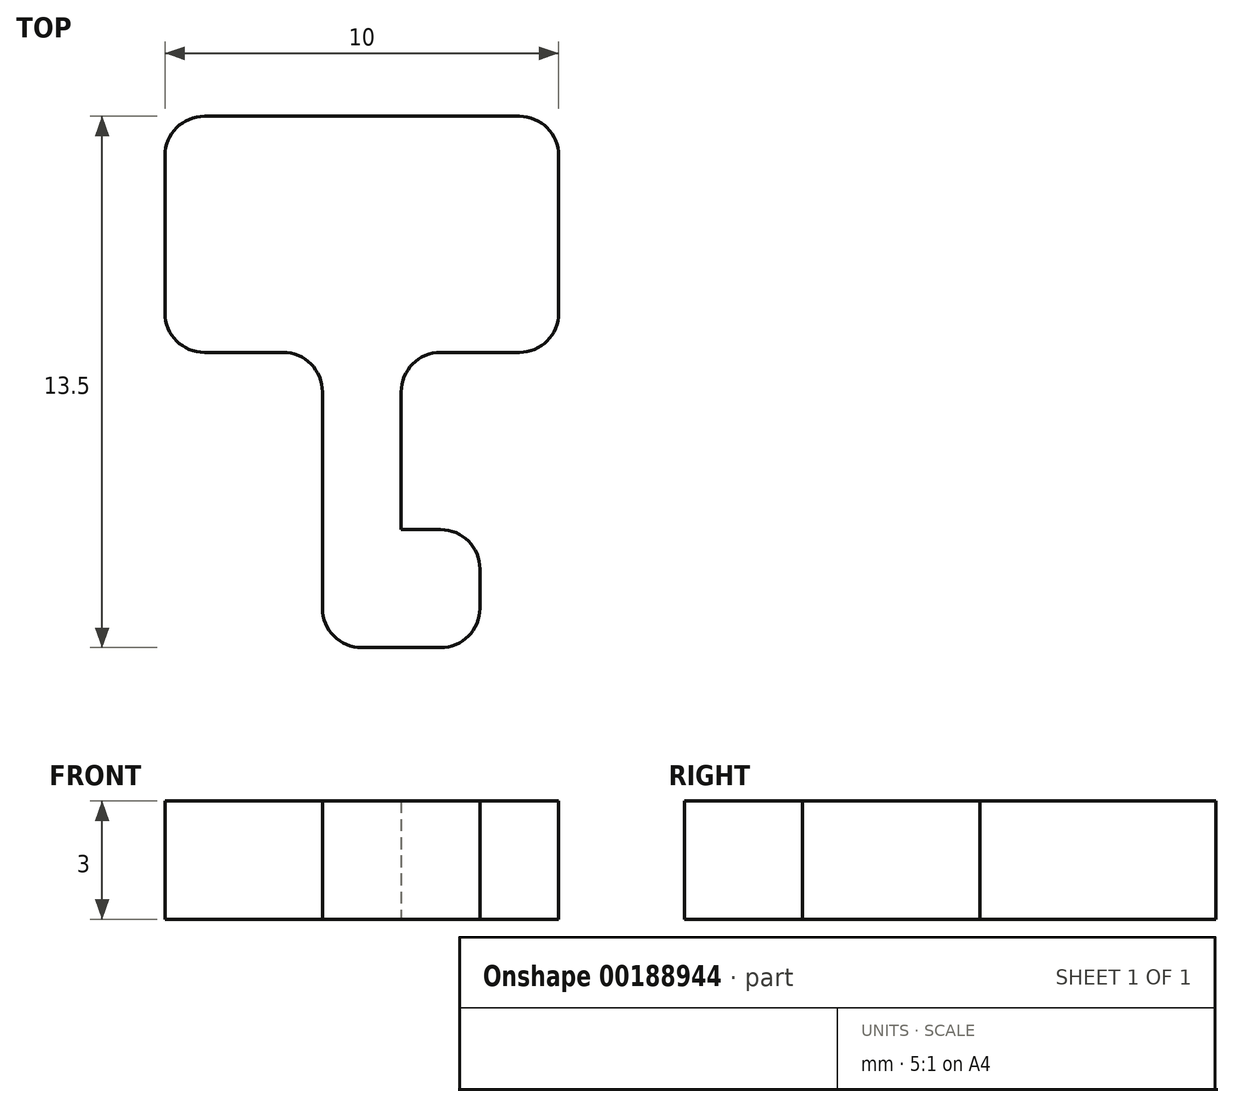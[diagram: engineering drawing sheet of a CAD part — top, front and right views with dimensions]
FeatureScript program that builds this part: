
annotation { "Feature Type Name" : "Feature", "Feature Type Description" : "" }
export const myFeature = defineFeature(function(context is Context, id is Id, definition is map)
    precondition{}
    {
        {
            var Q0;
            Q0=qCreatedBy(makeId("Top.planeOp"),FACE);
            var sketch = newSketch(context, id + "F0", { "sketchPlane" : qUnion([Q0])});
            skLineSegment(sketch, "E0", {"start": v(-1, 0) * mm, "end": v(-3, 0) * mm});
            skLineSegment(sketch, "E1", {"start": v(-4, -1) * mm, "end": v(-4, -4.5) * mm});
            skLineSegment(sketch, "E2", {"start": v(-4, -4.5) * mm, "end": v(-3, -4.5) * mm});
            skLineSegment(sketch, "E3", {"start": v(-2, -5.5) * mm, "end": v(-2, -6.5) * mm});
            skLineSegment(sketch, "E4", {"start": v(-6, -6.5) * mm, "end": v(-6, -1) * mm});
            skLineSegment(sketch, "E5", {"start": v(-7, 0) * mm, "end": v(-9, 0) * mm});
            skLineSegment(sketch, "E6", {"start": v(-10, 1) * mm, "end": v(-10, 5) * mm});
            skLineSegment(sketch, "E7", {"start": v(-9, 6) * mm, "end": v(-1, 6) * mm});
            skLineSegment(sketch, "E8", {"start": v(0, 5) * mm, "end": v(0, 1) * mm});
            skLineSegment(sketch, "E9", {"start": v(-5, -7.5) * mm, "end": v(-3, -7.5) * mm});
            skPoint(sketch, "E10.visualSharp", {"position": v(-6, 0) * mm});
            skArc(sketch, "E10.filletArc", {"start": v(-6, -1) * mm, "mid": v(-6.3, -0.3) * mm, "end": v(-7, 0) * mm});
            skPoint(sketch, "E11.visualSharp", {"position": v(-4, 0) * mm});
            skArc(sketch, "E11.filletArc", {"start": v(-3, 0) * mm, "mid": v(-3.7, -0.3) * mm, "end": v(-4, -1) * mm});
            skPoint(sketch, "E12.visualSharp", {"position": v(0, 0) * mm});
            skArc(sketch, "E12.filletArc", {"start": v(-1, 0) * mm, "mid": v(-0.3, 0.3) * mm, "end": v(0, 1) * mm});
            skPoint(sketch, "E13.visualSharp", {"position": v(0, 6) * mm});
            skArc(sketch, "E13.filletArc", {"start": v(0, 5) * mm, "mid": v(-0.3, 5.7) * mm, "end": v(-1, 6) * mm});
            skPoint(sketch, "E14.visualSharp", {"position": v(-10, 6) * mm});
            skArc(sketch, "E14.filletArc", {"start": v(-9, 6) * mm, "mid": v(-9.7, 5.7) * mm, "end": v(-10, 5) * mm});
            skPoint(sketch, "E15.visualSharp", {"position": v(-10, 0) * mm});
            skArc(sketch, "E15.filletArc", {"start": v(-10, 1) * mm, "mid": v(-9.7, 0.3) * mm, "end": v(-9, 0) * mm});
            skPoint(sketch, "E16.visualSharp", {"position": v(-2, -4.5) * mm});
            skArc(sketch, "E16.filletArc", {"start": v(-2, -5.5) * mm, "mid": v(-2.3, -4.8) * mm, "end": v(-3, -4.5) * mm});
            skPoint(sketch, "E17.visualSharp", {"position": v(-6, -7.5) * mm});
            skArc(sketch, "E17.filletArc", {"start": v(-6, -6.5) * mm, "mid": v(-5.7, -7.2) * mm, "end": v(-5, -7.5) * mm});
            skPoint(sketch, "E18.visualSharp", {"position": v(-2, -7.5) * mm});
            skArc(sketch, "E18.filletArc", {"start": v(-3, -7.5) * mm, "mid": v(-2.3, -7.2) * mm, "end": v(-2, -6.5) * mm});
            skSolve(sketch);
        }
        {
            var Q0;
            Q0 = qSketchRegion(id + "F0", true);
            extrude(context, id + "F1", {"entities" : qUnion([Q0]), "depth" : 3 * mm});
        }
    });
